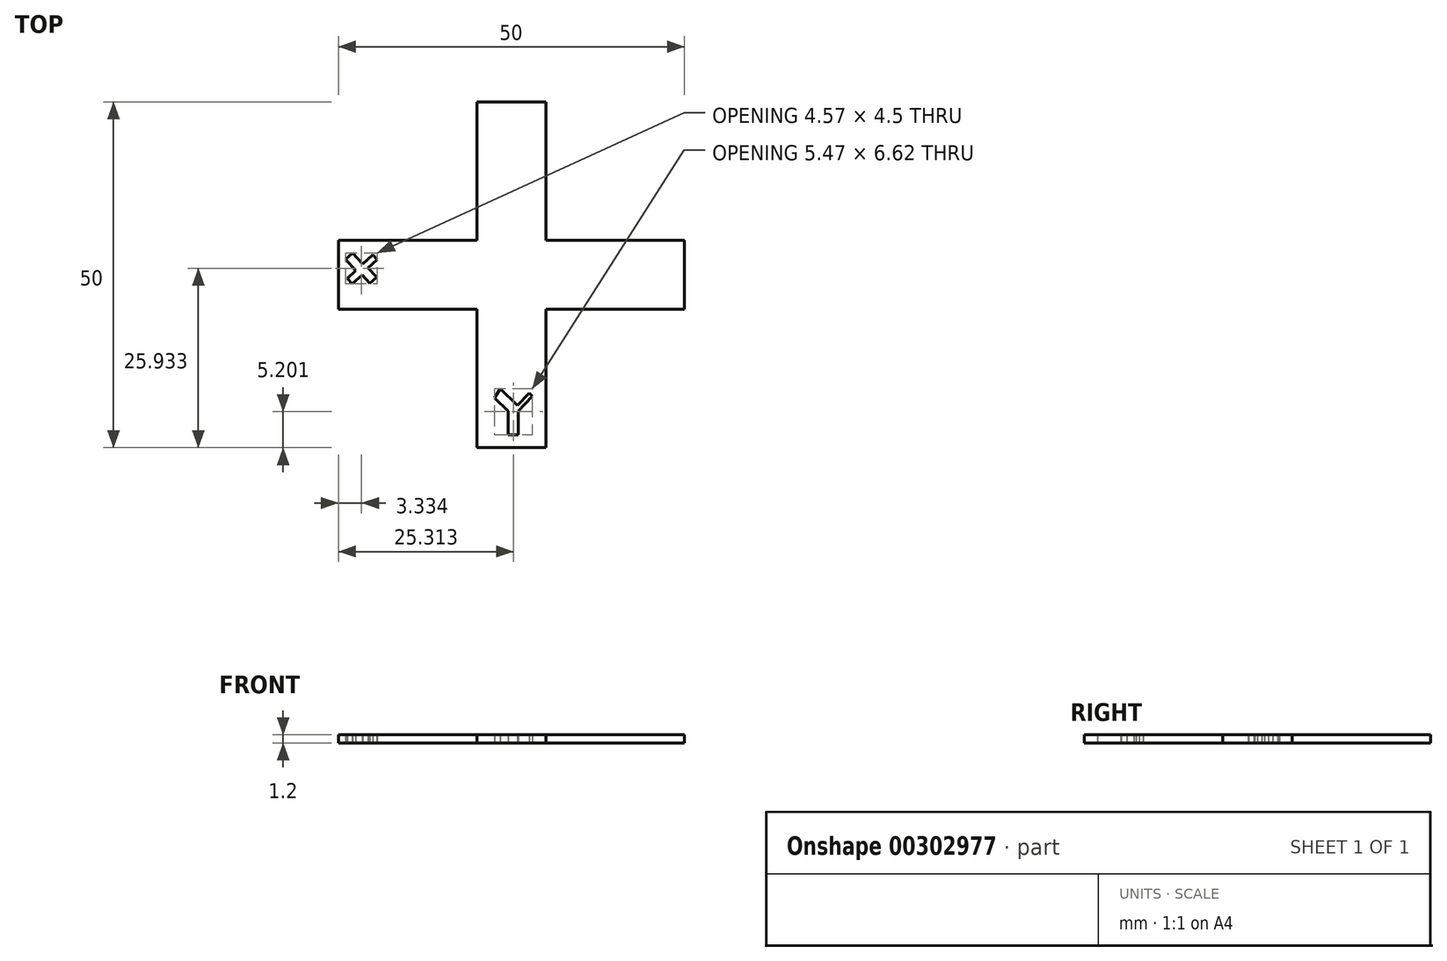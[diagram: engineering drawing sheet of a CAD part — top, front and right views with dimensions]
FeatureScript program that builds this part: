
annotation { "Feature Type Name" : "Feature", "Feature Type Description" : "" }
export const myFeature = defineFeature(function(context is Context, id is Id, definition is map)
    precondition{}
    {
        {
            var Q0;
            Q0=qCreatedBy(makeId("Top.planeOp"),FACE);
            var sketch = newSketch(context, id + "F0", { "sketchPlane" : qUnion([Q0])});
            skLineSegment(sketch, "E0.bottom", {"start": v(5, 25) * mm, "end": v(-5, 25) * mm});
            skLineSegment(sketch, "E0.top", {"start": v(5, -25) * mm, "end": v(-5, -25) * mm});
            skLineSegment(sketch, "E0.left", {"start": v(5, 25) * mm, "end": v(5, -25) * mm});
            skLineSegment(sketch, "E0.right", {"start": v(-5, 25) * mm, "end": v(-5, -25) * mm});
            skPoint(sketch, "E0.middle", {"position": v(0, 0) * mm});
            skLineSegment(sketch, "E1.bottom", {"start": v(-25, 5) * mm, "end": v(25, 5) * mm});
            skLineSegment(sketch, "E1.top", {"start": v(-25, -5) * mm, "end": v(25, -5) * mm});
            skLineSegment(sketch, "E1.left", {"start": v(-25, 5) * mm, "end": v(-25, -5) * mm});
            skLineSegment(sketch, "E1.right", {"start": v(25, 5) * mm, "end": v(25, -5) * mm});
            skLineSegment(sketch, "E2", {"start": v(-23.6, 2.56) * mm, "end": v(-22.92, 3.18) * mm});
            skLineSegment(sketch, "E3", {"start": v(-22.92, 3.18) * mm, "end": v(-21.46, 1.57) * mm});
            skLineSegment(sketch, "E4", {"start": v(-21.46, 1.57) * mm, "end": v(-20, 2.9) * mm});
            skLineSegment(sketch, "E5", {"start": v(-20, 2.9) * mm, "end": v(-19.38, 2.21) * mm});
            skLineSegment(sketch, "E6", {"start": v(-19.38, 2.21) * mm, "end": v(-20.71, 1) * mm});
            skLineSegment(sketch, "E7", {"start": v(-20.71, 1) * mm, "end": v(-19.47, -0.36) * mm});
            skLineSegment(sketch, "E8", {"start": v(-19.47, -0.36) * mm, "end": v(-20.44, -1.24) * mm});
            skLineSegment(sketch, "E9", {"start": v(-20.44, -1.24) * mm, "end": v(-21.57, 0) * mm});
            skLineSegment(sketch, "E10", {"start": v(-21.57, 0) * mm, "end": v(-23.02, -1.31) * mm});
            skLineSegment(sketch, "E11", {"start": v(-23.02, -1.31) * mm, "end": v(-23.74, -0.52) * mm});
            skLineSegment(sketch, "E12", {"start": v(-23.74, -0.52) * mm, "end": v(-22.48, 0.63) * mm});
            skLineSegment(sketch, "E13", {"start": v(-22.48, 0.63) * mm, "end": v(-23.95, 2.24) * mm});
            skLineSegment(sketch, "E14", {"start": v(-23.95, 2.24) * mm, "end": v(-23.6, 2.56) * mm});
            skLineSegment(sketch, "E15", {"start": v(-2.42, -17.83) * mm, "end": v(-0.48, -19.7) * mm});
            skLineSegment(sketch, "E16", {"start": v(-0.48, -19.7) * mm, "end": v(-0.48, -23.1) * mm});
            skLineSegment(sketch, "E17", {"start": v(-0.48, -23.1) * mm, "end": v(1, -23.1) * mm});
            skLineSegment(sketch, "E18", {"start": v(1, -23.1) * mm, "end": v(1, -19.73) * mm});
            skLineSegment(sketch, "E19", {"start": v(1, -19.73) * mm, "end": v(3.05, -17.56) * mm});
            skLineSegment(sketch, "E20", {"start": v(3.05, -17.56) * mm, "end": v(2.57, -17.1) * mm});
            skLineSegment(sketch, "E21", {"start": v(2.57, -17.1) * mm, "end": v(0.9, -18.88) * mm});
            skLineSegment(sketch, "E22", {"start": v(0.9, -18.88) * mm, "end": v(-1.63, -16.5) * mm});
            skLineSegment(sketch, "E23", {"start": v(-1.63, -16.5) * mm, "end": v(-2.42, -17.83) * mm});
            skSolve(sketch);
        }
        {
            var Q0;
            {var subQ5=sQuery(id+"F0.wireOp",EDGE,"E1.left");Q0=makeQuery(id+"F0.imprint","IMPRINT",FACE,{"disambiguationData":[TD([[makeQuery(id+"F0.imprint","IMPRINT",EDGE,{"derivedFrom":subQ5}),1.0]])]});}
            var Q1;
            {var subQ0=sQuery(id+"F0.wireOp",EDGE,"E1.bottom");var subQ1=sQuery(id+"F0.wireOp",EDGE,"E0.left");var subQ2=makeQuery(id+"F0.imprint","INTERSECT",VERTEX,{"derivedFrom":[subQ1,subQ0]});Q1=makeQuery(id+"F0.imprint","IMPRINT",FACE,{"disambiguationData":[TD([[makeQuery(id+"F0.imprint","IMPRINT",EDGE,{"disambiguationData":[TD([[subQ2,-1.0]])],"derivedFrom":subQ1}),-1.0]])]});}
            var Q2;
            {var subQ5=sQuery(id+"F0.wireOp",EDGE,"E1.right");Q2=makeQuery(id+"F0.imprint","IMPRINT",FACE,{"disambiguationData":[TD([[makeQuery(id+"F0.imprint","IMPRINT",EDGE,{"derivedFrom":subQ5}),-1.0]])]});}
            var Q3;
            {var subQ0=sQuery(id+"F0.wireOp",EDGE,"E0.bottom");Q3=makeQuery(id+"F0.imprint","IMPRINT",FACE,{"disambiguationData":[TD([[makeQuery(id+"F0.imprint","IMPRINT",EDGE,{"derivedFrom":subQ0}),1.0]])]});}
            var Q4;
            {var subQ1=sQuery(id+"F0.wireOp",EDGE,"E0.top");Q4=makeQuery(id+"F0.imprint","IMPRINT",FACE,{"disambiguationData":[TD([[makeQuery(id+"F0.imprint","IMPRINT",EDGE,{"derivedFrom":subQ1}),-1.0]])]});}
            extrude(context, id + "F1", {"entities" : qUnion([Q0, Q1, Q2, Q3, Q4]), "depth" : 1.2 * mm, "offsetDistance" : 25 * mm});
        }
    });
